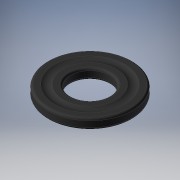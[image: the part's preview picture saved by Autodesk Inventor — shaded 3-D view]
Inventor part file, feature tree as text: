
AUTODESK INVENTOR PART (.ipt)
format: ipt  version: 2019 (Build 230136000, 136)  size: 195,072 bytes
history: native  units: mm
features: other x77, revolve x1, sketch x1
ambient origin geometry x8: Origin, YZ Plane, XZ Plane, XY Plane, X Axis, Y Axis, Z Axis, Center Point
bodies: Solid1 (feature_tree)
feature tree (79):
  revolve  "Revolution1"  [1 undecoded]
  other  "HW_B_1_XY"
  other  "HW_B_1_YZ"
  other  "HW_B_1_ZX"
  other  "HW_B_1_X"
  other  "HW_B_1_Y"
  other  "HW_B_1_Z"
  other  "HW_B_1_Center"
  other  "HW_B_10_XY"
  other  "HW_B_10_YZ"
  other  "HW_B_10_ZX"
  other  "HW_B_10_X"
  other  "HW_B_10_Y"
  other  "HW_B_10_Z"
  other  "HW_B_10_Center"
  other  "HW_B_2_XY"
  other  "HW_B_2_YZ"
  other  "HW_B_2_ZX"
  other  "HW_B_2_X"
  other  "HW_B_2_Y"
  other  "HW_B_2_Z"
  other  "HW_B_2_Center"
  other  "HW_B_3_XY"
  other  "HW_B_3_YZ"
  other  "HW_B_3_ZX"
  other  "HW_B_3_X"
  other  "HW_B_3_Y"
  other  "HW_B_3_Z"
  other  "HW_B_3_Center"
  other  "HW_B_4_XY"
  other  "HW_B_4_YZ"
  other  "HW_B_4_ZX"
  other  "HW_B_4_X"
  other  "HW_B_4_Y"
  other  "HW_B_4_Z"
  other  "HW_B_4_Center"
  other  "HW_B_5_XY"
  other  "HW_B_5_YZ"
  other  "HW_B_5_ZX"
  other  "HW_B_5_X"
  other  "HW_B_5_Y"
  other  "HW_B_5_Z"
  other  "HW_B_5_Center"
  other  "HW_B_6_XY"
  other  "HW_B_6_YZ"
  other  "HW_B_6_ZX"
  other  "HW_B_6_X"
  other  "HW_B_6_Y"
  other  "HW_B_6_Z"
  other  "HW_B_6_Center"
  other  "HW_B_7_XY"
  other  "HW_B_7_YZ"
  other  "HW_B_7_ZX"
  other  "HW_B_7_X"
  other  "HW_B_7_Y"
  other  "HW_B_7_Z"
  other  "HW_B_7_Center"
  other  "HW_B_8_XY"
  other  "HW_B_8_YZ"
  other  "HW_B_8_ZX"
  other  "HW_B_8_X"
  other  "HW_B_8_Y"
  other  "HW_B_8_Z"
  other  "HW_B_8_Center"
  other  "HW_B_9_XY"
  other  "HW_B_9_YZ"
  other  "HW_B_9_ZX"
  other  "HW_B_9_X"
  other  "HW_B_9_Y"
  other  "HW_B_9_Z"
  other  "HW_B_9_Center"
  other  "HW_SW_XY"
  other  "HW_SW_YZ"
  other  "HW_SW_ZX"
  other  "HW_SW_X"
  other  "HW_SW_Y"
  other  "HW_SW_Z"
  other  "HW_SW_Center"
  sketch  "Sketch_1"  dims[d0=360.0deg d1=0.0mm]
note: 1 required parameter value undecoded (feature->parameter linkage not recoverable at this tier; creation-order binding heuristic only, values carry confidence <= 0.55)
